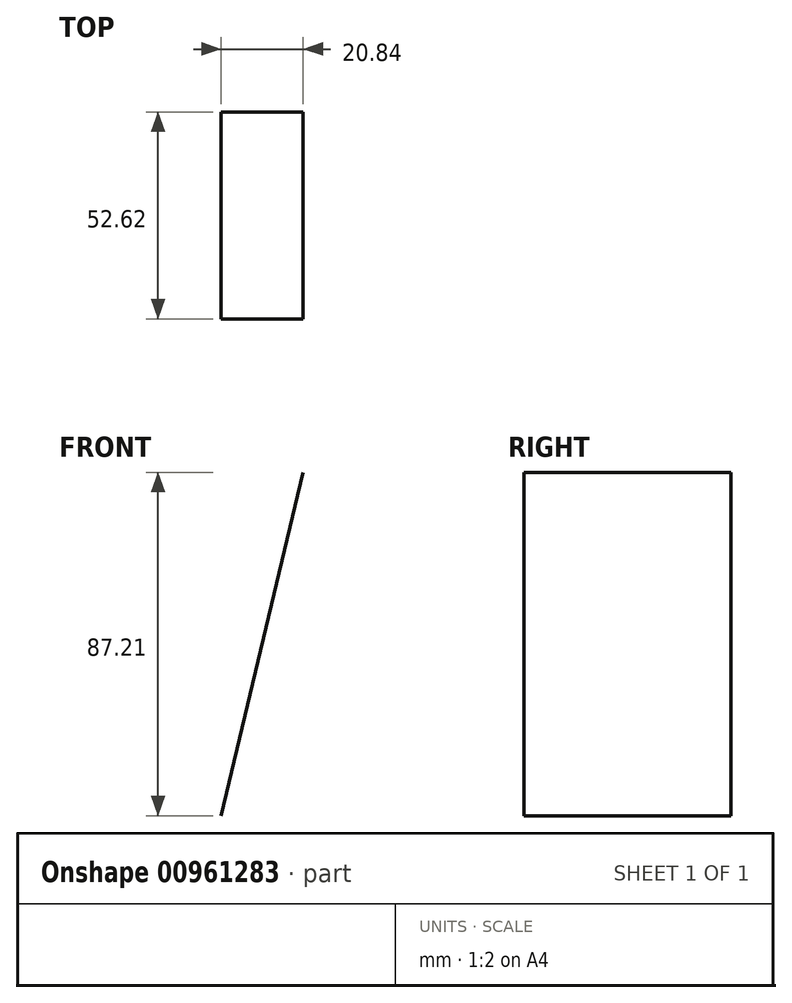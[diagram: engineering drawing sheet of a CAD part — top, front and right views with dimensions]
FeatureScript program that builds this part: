
annotation { "Feature Type Name" : "Feature", "Feature Type Description" : "" }
export const myFeature = defineFeature(function(context is Context, id is Id, definition is map)
    precondition{}
    {
        {
            var Q0;
            Q0=qCreatedBy(makeId("Front.planeOp"),FACE);
            var sketch = newSketch(context, id + "F0", { "sketchPlane" : qUnion([Q0])});
            skLineSegment(sketch, "E0", {"start": v(-89.6, 87.2) * mm, "end": v(92.7, 87.2) * mm});
            skLineSegment(sketch, "E1", {"start": v(92.7, 87.2) * mm, "end": v(0, 0) * mm});
            skLineSegment(sketch, "E2", {"start": v(0, 0) * mm, "end": v(-110.43, 0) * mm});
            skLineSegment(sketch, "E3", {"start": v(-110.43, 0) * mm, "end": v(-89.6, 87.2) * mm});
            skSolve(sketch);
        }
        {
            var Q0;
            Q0=makeQuery(id+"F0.imprint","IMPRINT",FACE,{"disambiguationData":[TD([[makeQuery(id+"F0.imprint","IMPRINT",EDGE,{"derivedFrom":sQuery(id+"F0.wireOp",EDGE,"E0")}),-1.0]])]});
            var Q1;
            Q1=sQuery(id+"F0.wireOp",EDGE,"E3");
            extrude(context, id + "F1", {"entities" : qUnion([Q0]), "bodyType" : ToolBodyType.SURFACE, "surfaceEntities" : qUnion([Q1]), "depth" : 52.62 * mm, "offsetDistance" : 25.4 * mm});
        }
    });
